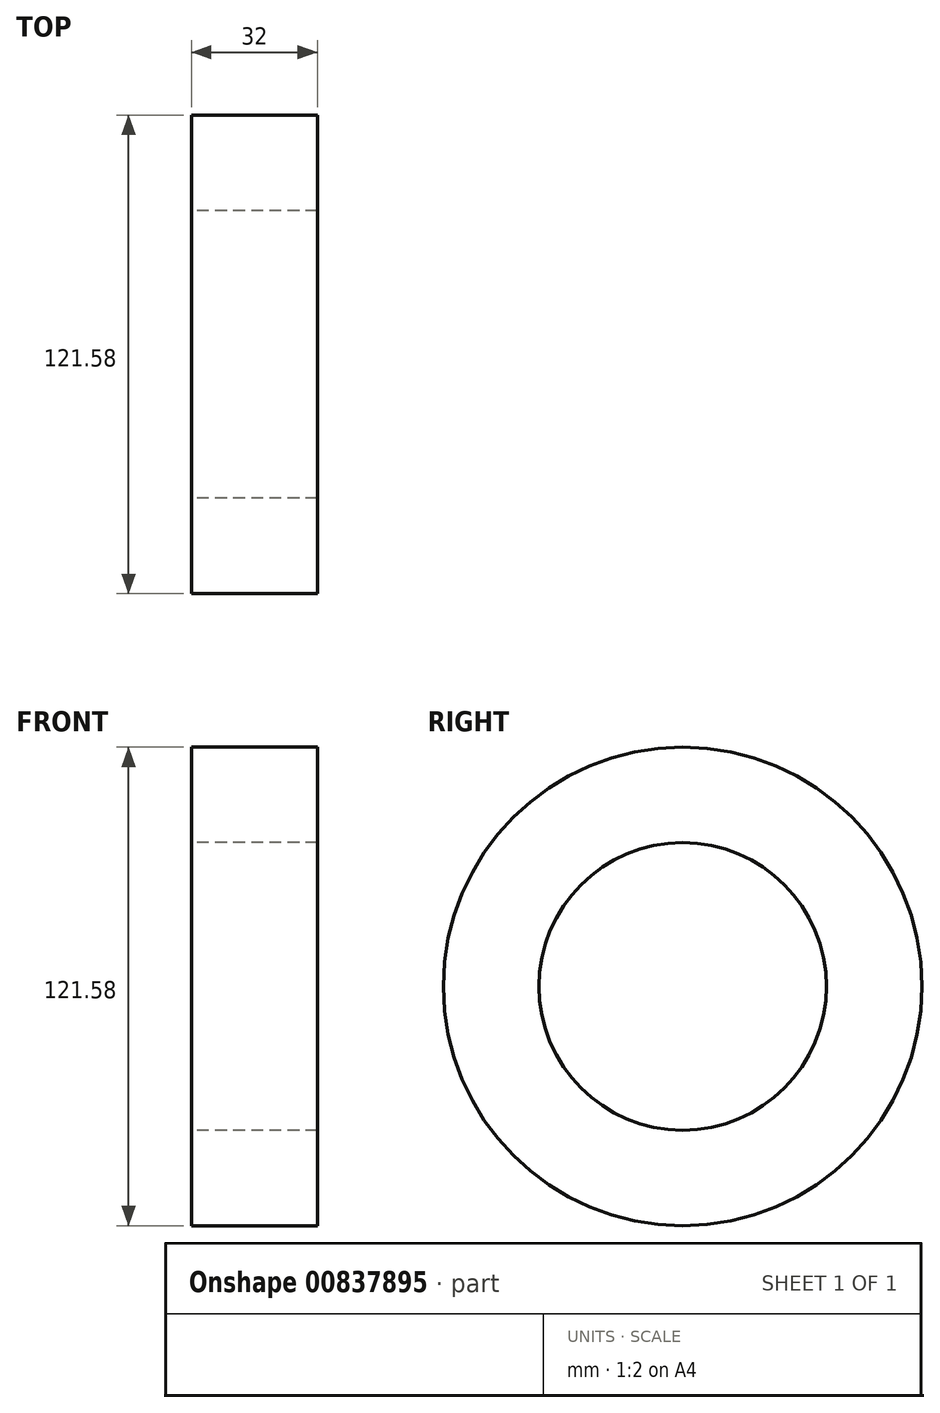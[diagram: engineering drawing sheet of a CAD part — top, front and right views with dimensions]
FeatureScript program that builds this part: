
annotation { "Feature Type Name" : "Feature", "Feature Type Description" : "" }
export const myFeature = defineFeature(function(context is Context, id is Id, definition is map)
    precondition{}
    {
        {
            var Q0;
            Q0=qCreatedBy(makeId("Right.planeOp"),FACE);
            var sketch = newSketch(context, id + "F0", { "sketchPlane" : qUnion([Q0])});
            skCircle(sketch, "E0", {"center": v(0, 0) * mm, "radius": 60.8 * mm});
            skCircle(sketch, "E1", {"center": v(0, 0) * mm, "radius": 36.53 * mm});
            skSolve(sketch);
        }
        {
            var Q0;
            Q0=makeQuery(id+"F0.imprint","IMPRINT",FACE,{"disambiguationData":[TD([[makeQuery(id+"F0.imprint","IMPRINT",EDGE,{"derivedFrom":sQuery(id+"F0.wireOp",EDGE,"E0")}),1.0]])]});
            extrude(context, id + "F1", {"entities" : qUnion([Q0]), "depth" : 32 * mm, "offsetDistance" : 25 * mm});
        }
    });
